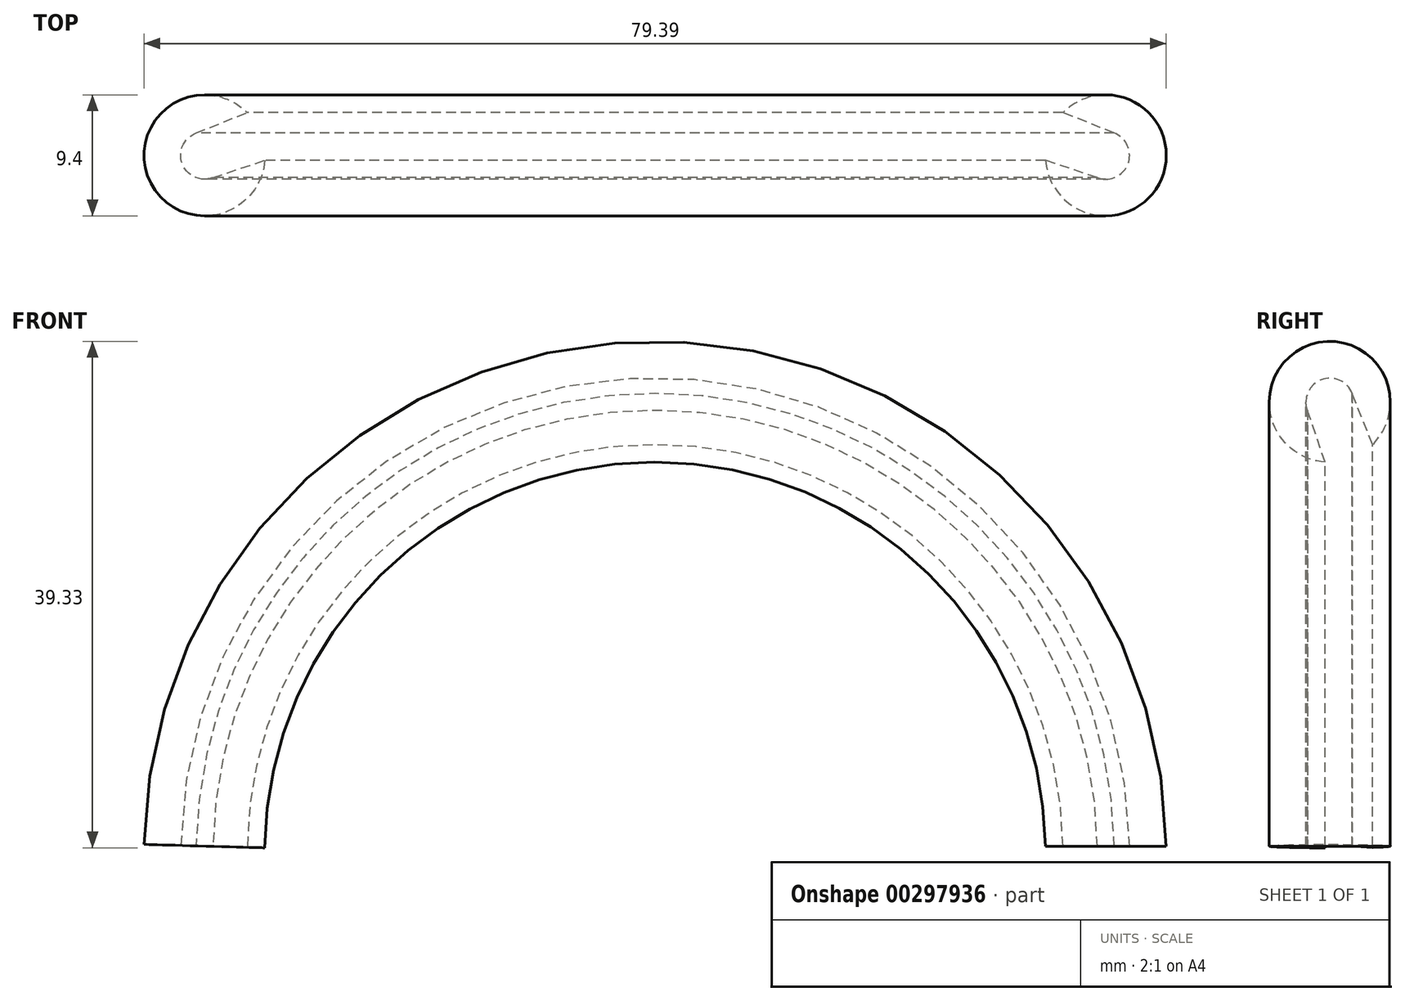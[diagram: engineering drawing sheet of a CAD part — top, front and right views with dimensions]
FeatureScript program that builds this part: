
annotation { "Feature Type Name" : "Feature", "Feature Type Description" : "" }
export const myFeature = defineFeature(function(context is Context, id is Id, definition is map)
    precondition{}
    {
        {
            var Q0;
            Q0=qCreatedBy(makeId("Top.planeOp"),FACE);
            var sketch = newSketch(context, id + "F0", { "sketchPlane" : qUnion([Q0])});
            skArc(sketch, "E0", {"start": v(-4.69, -0.37) * mm, "mid": v(4.4, -1.63) * mm, "end": v(-3.32, 3.33) * mm});
            skArc(sketch, "E1", {"start": v(-0.66, -1.73) * mm, "mid": v(1.73, -0.66) * mm, "end": v(0.66, 1.73) * mm});
            skLineSegment(sketch, "E2", {"start": v(0.66, 1.73) * mm, "end": v(-3.32, 3.33) * mm});
            skLineSegment(sketch, "E3", {"start": v(-0.66, -1.73) * mm, "end": v(-4.69, -0.37) * mm});
            skLineSegment(sketch, "E4", {"start": v(0.66, 1.73) * mm, "end": v(-0.66, -1.73) * mm, "construction": true});
            skSolve(sketch);
        }
        {
            var Q0;
            Q0=qCreatedBy(makeId("Front.planeOp"),FACE);
            var sketch = newSketch(context, id + "F1", { "sketchPlane" : qUnion([Q0])});
            skArc(sketch, "E5", {"start": v(0, 0) * mm, "mid": v(-35, 34.5) * mm, "end": v(-70, 0) * mm});
            skSolve(sketch);
        }
        {
            var Q0;
            Q0=makeQuery(id+"F0.imprint","IMPRINT",FACE,{"disambiguationData":[TD([[makeQuery(id+"F0.imprint","IMPRINT",EDGE,{"derivedFrom":sQuery(id+"F0.wireOp",EDGE,"E0")}),1.0]])]});
            var Q1;
            Q1=sQuery(id+"F1.wireOp",EDGE,"E5");
            sweep(context, id + "F2", {"profiles" : qUnion([Q0]), "path" : qUnion([Q1])});
        }
    });
